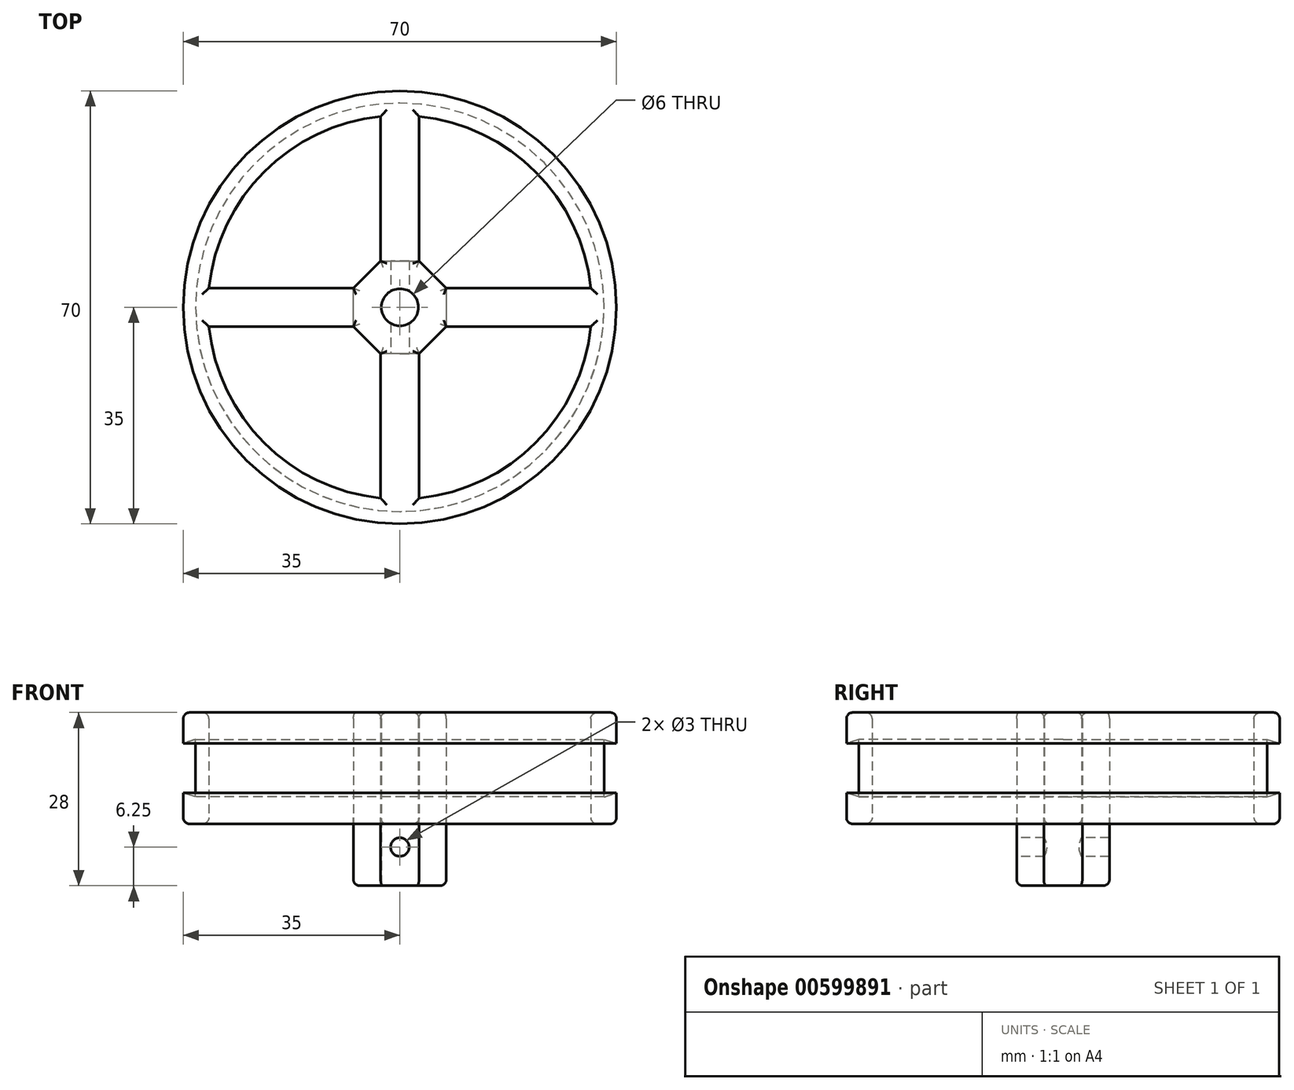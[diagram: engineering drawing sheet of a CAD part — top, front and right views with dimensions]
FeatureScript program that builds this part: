
annotation { "Feature Type Name" : "Feature", "Feature Type Description" : "" }
export const myFeature = defineFeature(function(context is Context, id is Id, definition is map)
    precondition{}
    {
        {
            var Q0;
            Q0=qCreatedBy(makeId("Top.planeOp"),FACE);
            var sketch = newSketch(context, id + "F0", { "sketchPlane" : qUnion([Q0])});
            skCircle(sketch, "E0", {"center": v(0, 0) * mm, "radius": 35 * mm});
            skCircle(sketch, "E1", {"center": v(0, 0) * mm, "radius": 31 * mm});
            skCircle(sketch, "E2.cCircle", {"center": v(0, 0) * mm, "radius": 7.5 * mm, "construction": true});
            skLineSegment(sketch, "E2.0", {"start": v(-7.5, 3.1) * mm, "end": v(-3.1, 7.5) * mm});
            skLineSegment(sketch, "E2.1", {"start": v(-3.1, 7.5) * mm, "end": v(3.1, 7.5) * mm});
            skLineSegment(sketch, "E2.2", {"start": v(3.1, 7.5) * mm, "end": v(7.5, 3.1) * mm});
            skLineSegment(sketch, "E2.3", {"start": v(7.5, 3.1) * mm, "end": v(7.5, -3.1) * mm});
            skLineSegment(sketch, "E2.4", {"start": v(7.5, -3.1) * mm, "end": v(3.1, -7.5) * mm});
            skLineSegment(sketch, "E2.5", {"start": v(3.1, -7.5) * mm, "end": v(-3.1, -7.5) * mm});
            skLineSegment(sketch, "E2.6", {"start": v(-3.1, -7.5) * mm, "end": v(-7.5, -3.1) * mm});
            skLineSegment(sketch, "E2.7", {"start": v(-7.5, -3.1) * mm, "end": v(-7.5, 3.1) * mm});
            skPoint(sketch, "E2.0.midPoint", {"position": v(-5.3, 5.3) * mm});
            skLineSegment(sketch, "E3", {"start": v(-7.5, 3.1) * mm, "end": v(-30.84, 3.1) * mm});
            skLineSegment(sketch, "E4", {"start": v(-7.5, -3.1) * mm, "end": v(-30.84, -3.1) * mm});
            skLineSegment(sketch, "E5", {"start": v(-3.1, -7.5) * mm, "end": v(-3.1, -30.84) * mm});
            skLineSegment(sketch, "E6", {"start": v(3.1, -7.5) * mm, "end": v(3.1, -30.84) * mm});
            skLineSegment(sketch, "E7", {"start": v(7.5, -3.1) * mm, "end": v(30.84, -3.1) * mm});
            skLineSegment(sketch, "E8", {"start": v(7.5, 3.1) * mm, "end": v(30.84, 3.1) * mm});
            skLineSegment(sketch, "E9", {"start": v(3.1, 7.5) * mm, "end": v(3.1, 30.84) * mm});
            skLineSegment(sketch, "E10", {"start": v(-3.1, 7.5) * mm, "end": v(-3.1, 30.84) * mm});
            skCircle(sketch, "E11", {"center": v(0, 0) * mm, "radius": 3 * mm});
            skSolve(sketch);
        }
        {
            var Q0;
            Q0=makeQuery(id+"F0.imprint","IMPRINT",FACE,{"disambiguationData":[TD([[makeQuery(id+"F0.imprint","IMPRINT",EDGE,{"derivedFrom":sQuery(id+"F0.wireOp",EDGE,"E0")}),1.0]])]});
            var Q1;
            Q1=makeQuery(id+"F0.imprint","IMPRINT",FACE,{"disambiguationData":[TD([[makeQuery(id+"F0.imprint","IMPRINT",EDGE,{"derivedFrom":sQuery(id+"F0.wireOp",EDGE,"G2GfLrx0-wZqf-QSxm-ZXgr-IlE5PP5L3oyy")}),-1.0]])]});
            var Q2;
            Q2=makeQuery(id+"F0.imprint","IMPRINT",FACE,{"disambiguationData":[TD([[makeQuery(id+"F0.imprint","IMPRINT",EDGE,{"derivedFrom":sQuery(id+"F0.wireOp",EDGE,"E2.3")}),1.0]])]});
            var Q3;
            Q3=makeQuery(id+"F0.imprint","IMPRINT",FACE,{"disambiguationData":[TD([[makeQuery(id+"F0.imprint","IMPRINT",EDGE,{"derivedFrom":sQuery(id+"F0.wireOp",EDGE,"E2.1")}),1.0]])]});
            var Q4;
            Q4=makeQuery(id+"F0.imprint","IMPRINT",FACE,{"disambiguationData":[TD([[makeQuery(id+"F0.imprint","IMPRINT",EDGE,{"derivedFrom":sQuery(id+"F0.wireOp",EDGE,"E2.7")}),1.0]])]});
            var Q5;
            Q5=makeQuery(id+"F0.imprint","IMPRINT",FACE,{"disambiguationData":[TD([[makeQuery(id+"F0.imprint","IMPRINT",EDGE,{"derivedFrom":sQuery(id+"F0.wireOp",EDGE,"E2.5")}),1.0]])]});
            var Q6;
            {var subQ0=sQuery(id+"F0.wireOp",EDGE,"4JRxjBNt-gD2a-U7DO-ra2H-WZyzhIXIm6s6");Q6=makeQuery(id+"F0.imprint","IMPRINT",FACE,{"disambiguationData":[TD([[makeQuery(id+"F0.imprint","IMPRINT",EDGE,{"derivedFrom":subQ0}),1.0]])]});}
            var Q7;
            Q7=makeQuery(id+"F0.imprint","IMPRINT",FACE,{"disambiguationData":[TD([[makeQuery(id+"F0.imprint","IMPRINT",EDGE,{"derivedFrom":sQuery(id+"F0.wireOp",EDGE,"E2.0")}),-1.0]])]});
            extrude(context, id + "F1", {"entities" : qUnion([Q0, Q1, Q2, Q3, Q4, Q5, Q6, Q7]), "depth" : 18 * mm, "offsetDistance" : 25 * mm});
        }
        {
            var Q0;
            Q0=makeQuery(id+"F0.imprint","IMPRINT",FACE,{"disambiguationData":[TD([[makeQuery(id+"F0.imprint","IMPRINT",EDGE,{"derivedFrom":sQuery(id+"F0.wireOp",EDGE,"G2GfLrx0-wZqf-QSxm-ZXgr-IlE5PP5L3oyy")}),-1.0]])]});
            var Q1;
            Q1=makeQuery(id+"F0.imprint","IMPRINT",FACE,{"disambiguationData":[TD([[makeQuery(id+"F0.imprint","IMPRINT",EDGE,{"derivedFrom":sQuery(id+"F0.wireOp",EDGE,"E2.0")}),-1.0]])]});
            extrude(context, id + "F2", {"entities" : qUnion([Q0, Q1]), "operationType" : NewBodyOperationType.ADD, "oppositeDirection" : true, "depth" : 10 * mm, "offsetDistance" : 25 * mm});
        }
        {
            var Q0;
            Q0=makeQuery(id+"F1.opExtrude","CAP_FACE",FACE,{"disambiguationData":[OSD([sQuery(id+"F0.wireOp",EDGE,"E0"),sQuery(id+"F0.wireOp",EDGE,"E1"),sQuery(id+"F0.wireOp",EDGE,"G2GfLrx0-wZqf-QSxm-ZXgr-IlE5PP5L3oyy"),sQuery(id+"F0.wireOp",EDGE,"E2.0"),sQuery(id+"F0.wireOp",EDGE,"E2.2"),sQuery(id+"F0.wireOp",EDGE,"E2.4"),sQuery(id+"F0.wireOp",EDGE,"E2.6"),sQuery(id+"F0.wireOp",EDGE,"E3"),sQuery(id+"F0.wireOp",EDGE,"E4"),sQuery(id+"F0.wireOp",EDGE,"E5"),sQuery(id+"F0.wireOp",EDGE,"E6"),sQuery(id+"F0.wireOp",EDGE,"E7"),sQuery(id+"F0.wireOp",EDGE,"E8"),sQuery(id+"F0.wireOp",EDGE,"E9"),sQuery(id+"F0.wireOp",EDGE,"E10"),sQuery(id+"F0.wireOp",EDGE,"hMq2OOA6-SgJz-HRXP-Au6y-u8avhN9kkdXA")])],"isStart":false});
            var Q1;
            Q1=makeQuery(id+"F2.opExtrude","CAP_EDGE",EDGE,{"disambiguationData":[OSD([sQuery(id+"F0.wireOp",EDGE,"E2.5")])],"isStart":false});
            var Q2;
            Q2=makeQuery(id+"F2.opExtrude","CAP_EDGE",EDGE,{"disambiguationData":[OSD([sQuery(id+"F0.wireOp",EDGE,"E2.4")])],"isStart":false});
            var Q3;
            Q3=makeQuery(id+"F2.opExtrude","CAP_EDGE",EDGE,{"disambiguationData":[OSD([sQuery(id+"F0.wireOp",EDGE,"E2.3")])],"isStart":false});
            var Q4;
            Q4=makeQuery(id+"F2.opExtrude","CAP_EDGE",EDGE,{"disambiguationData":[OSD([sQuery(id+"F0.wireOp",EDGE,"E2.2")])],"isStart":false});
            var Q5;
            Q5=makeQuery(id+"F2.opExtrude","CAP_EDGE",EDGE,{"disambiguationData":[OSD([sQuery(id+"F0.wireOp",EDGE,"E2.1")])],"isStart":false});
            var Q6;
            Q6=makeQuery(id+"F2.opExtrude","CAP_EDGE",EDGE,{"disambiguationData":[OSD([sQuery(id+"F0.wireOp",EDGE,"E2.0")])],"isStart":false});
            var Q7;
            Q7=makeQuery(id+"F2.opExtrude","CAP_EDGE",EDGE,{"disambiguationData":[OSD([sQuery(id+"F0.wireOp",EDGE,"E2.7")])],"isStart":false});
            var Q8;
            Q8=makeQuery(id+"F2.opExtrude","CAP_EDGE",EDGE,{"disambiguationData":[OSD([sQuery(id+"F0.wireOp",EDGE,"E2.6")])],"isStart":false});
            var Q9;
            Q9=makeQuery(id+"F1.opExtrude","CAP_EDGE",EDGE,{"disambiguationData":[OSD([sQuery(id+"F0.wireOp",EDGE,"E0")])],"isStart":true});
            var Q10;
            Q10=makeQuery(id+"F1.opExtrude","CAP_EDGE",EDGE,{"disambiguationData":[OSD([sQuery(id+"F0.wireOp",EDGE,"E10")])],"isStart":true});
            var Q11;
            Q11=makeQuery(id+"F1.opExtrude","CAP_EDGE",EDGE,{"disambiguationData":[OSD([sQuery(id+"F0.wireOp",EDGE,"E9")])],"isStart":true});
            var Q12;
            Q12=makeQuery(id+"F1.opExtrude","CAP_EDGE",EDGE,{"disambiguationData":[OSD([sQuery(id+"F0.wireOp",EDGE,"E8")])],"isStart":true});
            var Q13;
            Q13=makeQuery(id+"F1.opExtrude","CAP_EDGE",EDGE,{"disambiguationData":[OSD([sQuery(id+"F0.wireOp",EDGE,"E7")])],"isStart":true});
            var Q14;
            Q14=makeQuery(id+"F1.opExtrude","CAP_EDGE",EDGE,{"disambiguationData":[OSD([sQuery(id+"F0.wireOp",EDGE,"E6")])],"isStart":true});
            var Q15;
            Q15=makeQuery(id+"F1.opExtrude","CAP_EDGE",EDGE,{"disambiguationData":[OSD([sQuery(id+"F0.wireOp",EDGE,"E5")])],"isStart":true});
            var Q16;
            Q16=makeQuery(id+"F1.opExtrude","CAP_EDGE",EDGE,{"disambiguationData":[OSD([sQuery(id+"F0.wireOp",EDGE,"E4")])],"isStart":true});
            var Q17;
            {var subQ0=sQuery(id+"F0.wireOp",EDGE,"E1");Q17=makeQuery(id+"F1.opExtrude","CAP_EDGE",EDGE,{"disambiguationData":[OSD([subQ0]),TDD([makeQuery(id+"F0.imprint","IMPRINT",EDGE,{"disambiguationData":[TD([[makeQuery(id+"F0.imprint","INTERSECT",VERTEX,{"derivedFrom":[subQ0,sQuery(id+"F0.wireOp",EDGE,"E8")]}),-1.0]])],"derivedFrom":subQ0})])],"isStart":true});}
            var Q18;
            {var subQ0=sQuery(id+"F0.wireOp",EDGE,"E1");Q18=makeQuery(id+"F1.opExtrude","CAP_EDGE",EDGE,{"disambiguationData":[OSD([subQ0]),TDD([makeQuery(id+"F0.imprint","IMPRINT",EDGE,{"disambiguationData":[TD([[makeQuery(id+"F0.imprint","INTERSECT",VERTEX,{"derivedFrom":[subQ0,sQuery(id+"F0.wireOp",EDGE,"E6")]}),-1.0]])],"derivedFrom":subQ0})])],"isStart":true});}
            var Q19;
            {var subQ0=sQuery(id+"F0.wireOp",EDGE,"E1");Q19=makeQuery(id+"F1.opExtrude","CAP_EDGE",EDGE,{"disambiguationData":[OSD([subQ0]),TDD([makeQuery(id+"F0.imprint","IMPRINT",EDGE,{"disambiguationData":[TD([[makeQuery(id+"F0.imprint","INTERSECT",VERTEX,{"derivedFrom":[subQ0,sQuery(id+"F0.wireOp",EDGE,"E4")]}),-1.0]])],"derivedFrom":subQ0})])],"isStart":true});}
            var Q20;
            {var subQ0=sQuery(id+"F0.wireOp",EDGE,"E1");Q20=makeQuery(id+"F1.opExtrude","CAP_EDGE",EDGE,{"disambiguationData":[OSD([subQ0]),TDD([makeQuery(id+"F0.imprint","IMPRINT",EDGE,{"disambiguationData":[TD([[makeQuery(id+"F0.imprint","INTERSECT",VERTEX,{"derivedFrom":[subQ0,sQuery(id+"F0.wireOp",EDGE,"E3")]}),1.0]])],"derivedFrom":subQ0})])],"isStart":true});}
            var Q21;
            Q21=makeQuery(id+"F1.opExtrude","CAP_EDGE",EDGE,{"disambiguationData":[OSD([sQuery(id+"F0.wireOp",EDGE,"E2.0")])],"isStart":true});
            var Q22;
            Q22=makeQuery(id+"F1.opExtrude","CAP_EDGE",EDGE,{"disambiguationData":[OSD([sQuery(id+"F0.wireOp",EDGE,"E3")])],"isStart":true});
            var Q23;
            Q23=makeQuery(id+"F1.opExtrude","CAP_EDGE",EDGE,{"disambiguationData":[OSD([sQuery(id+"F0.wireOp",EDGE,"E2.6")])],"isStart":true});
            var Q24;
            Q24=makeQuery(id+"F1.opExtrude","CAP_EDGE",EDGE,{"disambiguationData":[OSD([sQuery(id+"F0.wireOp",EDGE,"E2.4")])],"isStart":true});
            var Q25;
            Q25=makeQuery(id+"F1.opExtrude","CAP_EDGE",EDGE,{"disambiguationData":[OSD([sQuery(id+"F0.wireOp",EDGE,"E2.2")])],"isStart":true});
            fillet(context, id + "F3", {"entities" : qUnion([Q0, Q1, Q2, Q3, Q4, Q5, Q6, Q7, Q8, Q9, Q10, Q11, Q12, Q13, Q14, Q15, Q16, Q17, Q18, Q19, Q20, Q21, Q22, Q23, Q24, Q25]), "radius" : 1 * mm, "tangentPropagation" : true, "allowEdgeOverflow" : false});
        }
        {
            var Q0;
            Q0=makeQuery(id+"F2.opExtrude","SWEPT_FACE",FACE,{"disambiguationData":[OSD([sQuery(id+"F0.wireOp",EDGE,"E2.1")])]});
            var sketch = newSketch(context, id + "F4", { "sketchPlane" : qUnion([Q0])});
            skPoint(sketch, "E12", {"position": v(0, -3.75) * mm});
            skSolve(sketch);
        }
        {
            var Q0;
            Q0=sQuery(id+"F4.wireOp",VERTEX,"E12");
            var Q1;
            Q1=makeQuery(id+"F1.opExtrude","SWEPT_BODY",BODY,{"disambiguationData":[OSD([sQuery(id+"F0.wireOp",EDGE,"E0"),sQuery(id+"F0.wireOp",EDGE,"E1"),sQuery(id+"F0.wireOp",EDGE,"E2.0"),sQuery(id+"F0.wireOp",EDGE,"E2.2"),sQuery(id+"F0.wireOp",EDGE,"E2.4"),sQuery(id+"F0.wireOp",EDGE,"E2.6"),sQuery(id+"F0.wireOp",EDGE,"E3"),sQuery(id+"F0.wireOp",EDGE,"E4"),sQuery(id+"F0.wireOp",EDGE,"E5"),sQuery(id+"F0.wireOp",EDGE,"E6"),sQuery(id+"F0.wireOp",EDGE,"E7"),sQuery(id+"F0.wireOp",EDGE,"E8"),sQuery(id+"F0.wireOp",EDGE,"E9"),sQuery(id+"F0.wireOp",EDGE,"E10"),sQuery(id+"F0.wireOp",EDGE,"E11")])]});
            hole(context, id + "F5", {"style" : HoleStyle.SIMPLE, "endStyle" : HoleEndStyle.THROUGH, "holeDiameter" : 3 * mm, "majorDiameter" : 5 * mm, "tappedDepth" : 12 * mm, "tapClearance" : 3, "locations" : qUnion([Q0]), "scope" : qUnion([Q1]), "startStyle" : HoleStartStyle.SKETCH});
        }
        {
            var Q0;
            Q0=qCreatedBy(makeId("Front.planeOp"),FACE);
            var sketch = newSketch(context, id + "F6", { "sketchPlane" : qUnion([Q0])});
            skLineSegment(sketch, "E13.bottom", {"start": v(-41, 13) * mm, "end": v(-33, 13) * mm});
            skLineSegment(sketch, "E13.top", {"start": v(-41, 5) * mm, "end": v(-33, 5) * mm});
            skLineSegment(sketch, "E13.left", {"start": v(-41, 13) * mm, "end": v(-41, 5) * mm});
            skLineSegment(sketch, "E13.right", {"start": v(-33, 13) * mm, "end": v(-33, 5) * mm});
            skPoint(sketch, "E14", {"position": v(-33, 9) * mm});
            skLineSegment(sketch, "E15", {"start": v(-33, 5) * mm, "end": v(-33, 4.35) * mm});
            skLineSegment(sketch, "E16", {"start": v(-33, 4.35) * mm, "end": v(-35.04, 5) * mm});
            skLineSegment(sketch, "E17", {"start": v(-35.04, 5) * mm, "end": v(-35.04, 13) * mm});
            skLineSegment(sketch, "E18", {"start": v(-35.04, 13) * mm, "end": v(-33, 13.67) * mm});
            skLineSegment(sketch, "E19", {"start": v(-33, 13.67) * mm, "end": v(-33, 13) * mm});
            skSolve(sketch);
        }
        {
            var Q0;
            Q0 = qSketchRegion(id + "F6", true);
            var Q1;
            {var subQ0=sQuery(id+"F0.wireOp",EDGE,"E11");Q1=makeQuery(id+"F3.opFillet","BLEND_EDGE",EDGE,{"blendedFrom":[makeQuery(id+"F1.opExtrude","CAP_EDGE",EDGE,{"disambiguationData":[OSD([subQ0])],"isStart":false}),makeQuery(id+"F2.boolean.opBoolean","MERGE",FACE,{"derivedFrom":[makeQuery(id+"F1.opExtrude","SWEPT_FACE",FACE,{"disambiguationData":[OSD([subQ0])]}),makeQuery(id+"F2.opExtrude","SWEPT_FACE",FACE,{"disambiguationData":[OSD([subQ0])]})]})],"blendedInto":[makeQuery(id+"F2.boolean.opBoolean","MERGE",FACE,{"derivedFrom":[makeQuery(id+"F1.opExtrude","SWEPT_FACE",FACE,{"disambiguationData":[OSD([subQ0])]}),makeQuery(id+"F2.opExtrude","SWEPT_FACE",FACE,{"disambiguationData":[OSD([subQ0])]})]})]});}
            revolve(context, id + "F7", {"operationType" : NewBodyOperationType.REMOVE, "surfaceOperationType" : NewSurfaceOperationType.NEW, "entities" : qUnion([Q0]), "axis" : qUnion([Q1]), "revolveType" : RevolveType.FULL, "oppositeDirection" : true});
        }
    });
